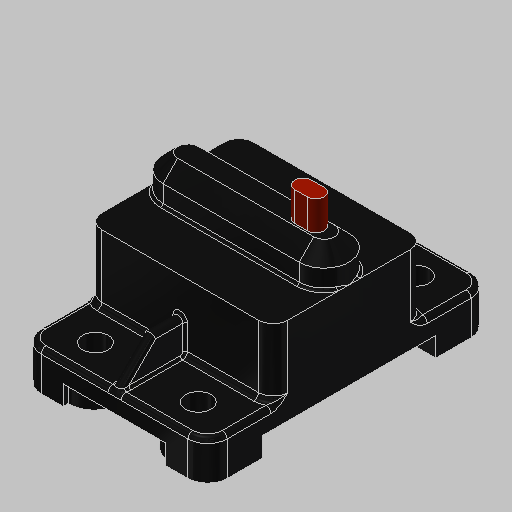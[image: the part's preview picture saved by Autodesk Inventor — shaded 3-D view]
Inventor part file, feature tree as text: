
AUTODESK INVENTOR PART (.ipt)
format: ipt  version: 2023.5 (Build 275446000, 446)  size: 385,536 bytes
history: native  units: mm (DEFAULTED — no unit token found)
features: fillet x7, extrude x6, mirror x3, chamfer x2, hole x1
ambient origin geometry x8: Origin, YZ Plane, XZ Plane, XY Plane, X Axis, Y Axis, Z Axis, Center Point
bodies: Solid1 (feature_tree)
feature tree (19):
  extrude  "Extrusion1"  Depth=48.26mm
  fillet  "Fillet1"  Radius=73.406mm
  extrude  "Extrusion2"  Depth=24.13mm
  fillet  "Fillet2"  Radius=36.703mm
  hole  "Hole1"  [1 undecoded]
  extrude  "Extrusion3"  Depth=5.08mm
  mirror  "Mirror3"
  mirror  "Mirror4"
  extrude  "Extrusion4"  Depth=39.37mm
  fillet  "Fillet3"  Radius=17.526mm
  chamfer  "Chamfer1"  Distance=3.81mm
  extrude  "Button"  Depth=10.795mm
  fillet  "Fillet4"  Radius=8.382mm
  fillet  "Fillet7"  Radius=14.224mm
  extrude  "Extrusion6"  Depth=14.224mm
  chamfer  "Chamfer2"  Distance=5.08mm
  fillet  "Fillet5"  Radius=12.954mm
  mirror  "Mirror5"
  fillet  "Fillet6"  Radius=8.89mm
note: 1 required parameter value undecoded (feature->parameter linkage not recoverable at this tier; creation-order binding heuristic only, values carry confidence <= 0.55)
